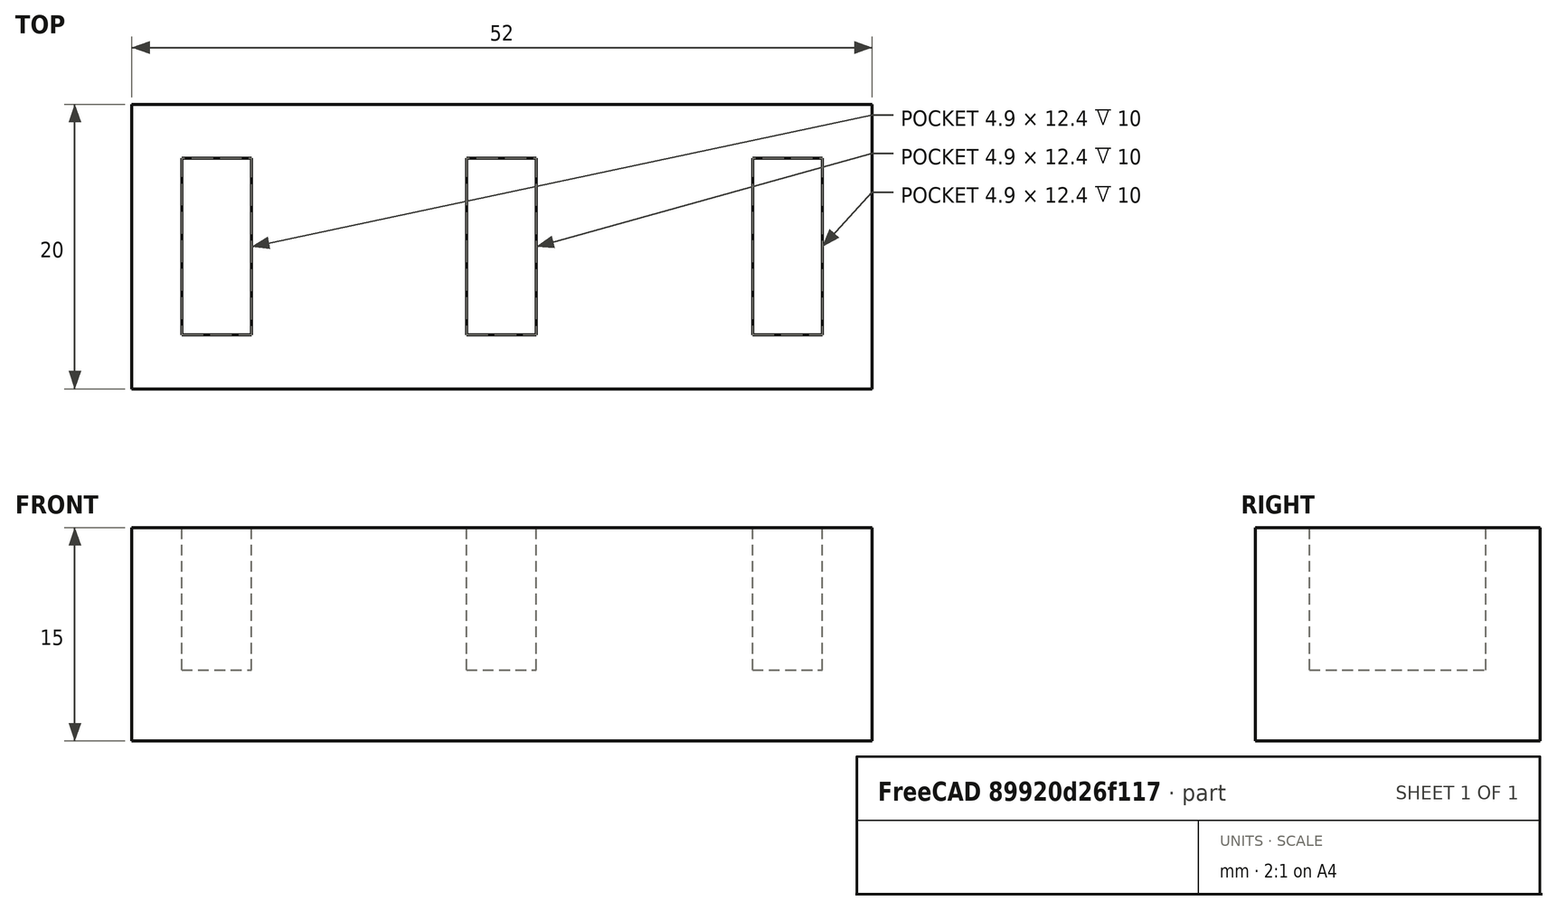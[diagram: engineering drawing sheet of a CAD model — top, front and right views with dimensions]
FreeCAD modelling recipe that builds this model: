
FCSTD DOCUMENT  (FreeCAD 0.20R29177 +233 (Git))
Label: portapendrives
License: Creative Commons Attribution-ShareAlike
LicenseURL: http://creativecommons.org/licenses/by-sa/4.0/
objects: Part::Box×4, Part::Cut×3
note: 7 computed .brp shape members not serialized (recipe doc carries the construction recipe); baked Part::Feature solids carry a one-line shape summary decoded from their .brp

FEATURE [Part::Box] Box  label="Cubo"
  AttacherType = Attacher::AttachEngine3D
  Height = 15
  Length = 52
  Width = 20
FEATURE [Part::Box] Box001  label="Cubo001"
  AttacherType = Attacher::AttachEngine3D
  Height = 15
  Length = 4.9
  Placement = pos=(3.5,3.8,5) rot=(0,0,1;0rad)
  Width = 12.4
FEATURE [Part::Box] Box002  label="Cubo002"
  AttacherType = Attacher::AttachEngine3D
  Height = 15
  Length = 4.9
  Placement = pos=(23.5,3.8,5) rot=(0,0,1;0rad)
  Width = 12.4
FEATURE [Part::Box] Box003  label="Cubo003"
  AttacherType = Attacher::AttachEngine3D
  Height = 15
  Length = 4.9
  Placement = pos=(43.6,3.8,5) rot=(0,0,1;0rad)
  Width = 12.4
FEATURE [Part::Cut] Cut
  Base = -> Box
  Refine = true
  Tool = -> Box001
FEATURE [Part::Cut] Cut001
  Base = -> Cut
  Refine = true
  Tool = -> Box002
FEATURE [Part::Cut] Cut002
  Base = -> Cut001
  Refine = true
  Tool = -> Box003
